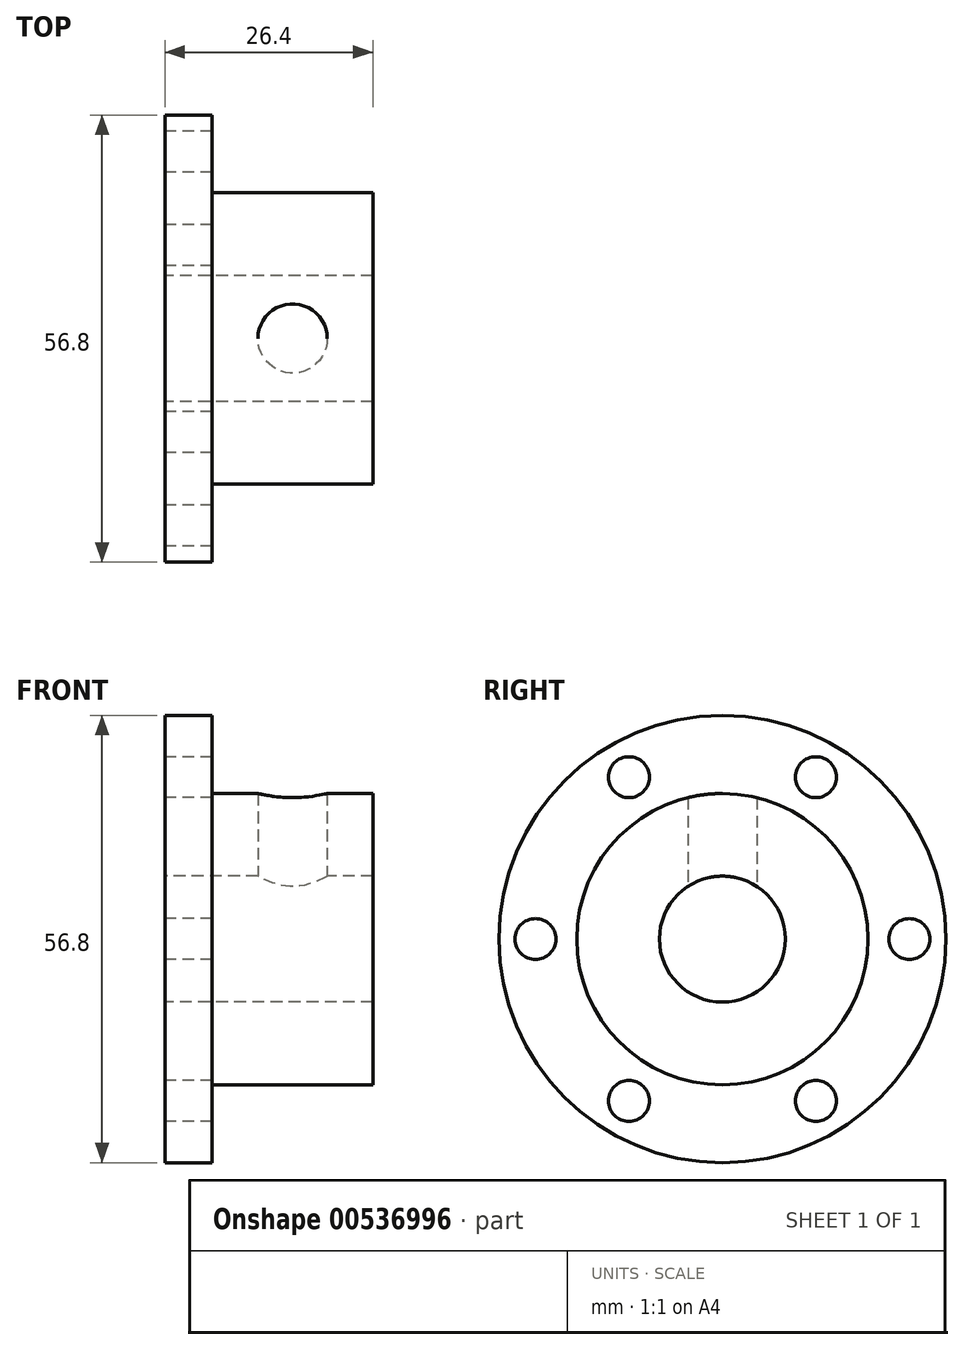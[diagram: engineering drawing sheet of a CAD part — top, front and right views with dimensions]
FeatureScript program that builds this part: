
annotation { "Feature Type Name" : "Feature", "Feature Type Description" : "" }
export const myFeature = defineFeature(function(context is Context, id is Id, definition is map)
    precondition{}
    {
        {
            var Q0;
            Q0=qCreatedBy(makeId("Front.planeOp"),FACE);
            var sketch = newSketch(context, id + "F0", { "sketchPlane" : qUnion([Q0])});
            skLineSegment(sketch, "E0", {"start": v(-27.35, -12.22) * mm, "end": v(29.45, -12.22) * mm});
            skSolve(sketch);
        }
        {
            var Q0;
            Q0=qCreatedBy(makeId("Front.planeOp"),FACE);
            var sketch = newSketch(context, id + "F1", { "sketchPlane" : qUnion([Q0])});
            skLineSegment(sketch, "E1.0", {"start": v(-27.35, -4.22) * mm, "end": v(-0.95, -4.22) * mm});
            skLineSegment(sketch, "E2.0", {"start": v(-21.35, 6.28) * mm, "end": v(-0.95, 6.28) * mm});
            skLineSegment(sketch, "E3.0", {"start": v(-27.35, 16.18) * mm, "end": v(-21.35, 16.18) * mm});
            skLineSegment(sketch, "E4", {"start": v(-27.35, 16.18) * mm, "end": v(-27.35, -4.22) * mm});
            skLineSegment(sketch, "E5.0", {"start": v(-21.35, 16.18) * mm, "end": v(-21.35, 6.28) * mm});
            skLineSegment(sketch, "E6.0", {"start": v(-0.95, 6.28) * mm, "end": v(-0.95, -4.22) * mm});
            skSolve(sketch);
        }
        {
            var Q0;
            Q0=makeQuery(id+"F1.imprint","IMPRINT",FACE,{"disambiguationData":[TD([[makeQuery(id+"F1.imprint","IMPRINT",EDGE,{"derivedFrom":sQuery(id+"F1.wireOp",EDGE,"E1.0")}),1.0]])]});
            var Q1;
            Q1=sQuery(id+"F0.wireOp",EDGE,"E0");
            revolve(context, id + "F2", {"entities" : qUnion([Q0]), "axis" : qUnion([Q1]), "revolveType" : RevolveType.FULL});
        }
        {
            var Q0;
            Q0=makeQuery(id+"F2.opRevolve","SWEPT_FACE",FACE,{"disambiguationData":[OSD([sQuery(id+"F1.wireOp",EDGE,"E4")])]});
            var sketch = newSketch(context, id + "F3", { "sketchPlane" : qUnion([Q0])});
            skLineSegment(sketch, "E7", {"start": v(0, -12.22) * mm, "end": v(23.75, -12.22) * mm});
            skCircle(sketch, "E8", {"center": v(23.75, -12.22) * mm, "radius": 2.6 * mm});
            skCircle(sketch, "E9.1.0", {"center": v(11.88, 8.35) * mm, "radius": 2.6 * mm});
            skCircle(sketch, "E9.2.0", {"center": v(-11.87, 8.35) * mm, "radius": 2.6 * mm});
            skCircle(sketch, "E9.3.0", {"center": v(-23.75, -12.22) * mm, "radius": 2.6 * mm});
            skCircle(sketch, "E9.4.0", {"center": v(-11.88, -32.79) * mm, "radius": 2.6 * mm});
            skCircle(sketch, "E9.5.0", {"center": v(11.88, -32.79) * mm, "radius": 2.6 * mm});
            skPoint(sketch, "E9.center", {"position": v(0, -12.22) * mm});
            skSolve(sketch);
        }
        {
            var Q0;
            Q0=makeQuery(id+"F3.imprint","IMPRINT",FACE,{"disambiguationData":[TD([[makeQuery(id+"F3.imprint","IMPRINT",EDGE,{"derivedFrom":sQuery(id+"F3.wireOp",EDGE,"E9.2.0")}),1.0]])]});
            var Q1;
            Q1=makeQuery(id+"F3.imprint","IMPRINT",FACE,{"disambiguationData":[TD([[makeQuery(id+"F3.imprint","IMPRINT",EDGE,{"derivedFrom":sQuery(id+"F3.wireOp",EDGE,"E9.3.0")}),1.0]])]});
            var Q2;
            Q2=makeQuery(id+"F3.imprint","IMPRINT",FACE,{"disambiguationData":[TD([[makeQuery(id+"F3.imprint","IMPRINT",EDGE,{"derivedFrom":sQuery(id+"F3.wireOp",EDGE,"E9.4.0")}),1.0]])]});
            var Q3;
            Q3=makeQuery(id+"F3.imprint","IMPRINT",FACE,{"disambiguationData":[TD([[makeQuery(id+"F3.imprint","IMPRINT",EDGE,{"derivedFrom":sQuery(id+"F3.wireOp",EDGE,"E9.5.0")}),1.0]])]});
            var Q4;
            Q4=makeQuery(id+"F3.imprint","IMPRINT",FACE,{"disambiguationData":[TD([[makeQuery(id+"F3.imprint","IMPRINT",EDGE,{"derivedFrom":sQuery(id+"F3.wireOp",EDGE,"E8")}),1.0]])]});
            var Q5;
            Q5=makeQuery(id+"F3.imprint","IMPRINT",FACE,{"disambiguationData":[TD([[makeQuery(id+"F3.imprint","IMPRINT",EDGE,{"derivedFrom":sQuery(id+"F3.wireOp",EDGE,"E9.1.0")}),1.0]])]});
            extrude(context, id + "F4", {"entities" : qUnion([Q0, Q1, Q2, Q3, Q4, Q5]), "operationType" : NewBodyOperationType.REMOVE, "endBound" : BoundingType.THROUGH_ALL, "oppositeDirection" : true, "depth" : 25 * mm, "offsetDistance" : 25 * mm});
        }
        {
            var Q0;
            Q0=qCreatedBy(makeId("Top.planeOp"),FACE);
            var sketch = newSketch(context, id + "F5", { "sketchPlane" : qUnion([Q0])});
            skLineSegment(sketch, "E10", {"start": v(-0.95, 0) * mm, "end": v(-11.15, 0) * mm});
            skCircle(sketch, "E11", {"center": v(-11.15, 0) * mm, "radius": 4 * mm});
            skSolve(sketch);
        }
        {
            var Q0;
            Q0=sQuery(id+"F5.wireOp",VERTEX,"E11.center");
            var Q1;
            Q1=makeQuery(id+"F2.opRevolve","SWEPT_BODY",BODY,{"disambiguationData":[OSD([sQuery(id+"F1.wireOp",EDGE,"E1.0"),sQuery(id+"F1.wireOp",EDGE,"E2.0"),sQuery(id+"F1.wireOp",EDGE,"E3.0"),sQuery(id+"F1.wireOp",EDGE,"E4"),sQuery(id+"F1.wireOp",EDGE,"E5.0"),sQuery(id+"F1.wireOp",EDGE,"E6.0")])]});
            hole(context, id + "F6", {"style" : HoleStyle.SIMPLE, "endStyle" : HoleEndStyle.THROUGH, "oppositeDirection" : true, "standardTappedOrClearance" : lookupTablePath({ "standard" : "ISO", "fit" : "Normal", "size" : "M8", "type" : "Clearance" }), "standardBlindInLast" : lookupTablePath({ "fit" : "Standard", "standard" : "ISO", "size" : "M8", "type" : "Clearance" }), "holeDiameter" : 8.8 * mm, "isTappedThrough" : true, "tappedDepth" : 12 * mm, "tapClearance" : 3, "locations" : qUnion([Q0]), "scope" : qUnion([Q1])});
        }
        {
            var Q0;
            Q0=sQuery(id+"F5.wireOp",VERTEX,"E11.center");
            var Q1;
            Q1=makeQuery(id+"F2.opRevolve","SWEPT_BODY",BODY,{"disambiguationData":[OSD([sQuery(id+"F1.wireOp",EDGE,"E1.0"),sQuery(id+"F1.wireOp",EDGE,"E2.0"),sQuery(id+"F1.wireOp",EDGE,"E3.0"),sQuery(id+"F1.wireOp",EDGE,"E4"),sQuery(id+"F1.wireOp",EDGE,"E5.0"),sQuery(id+"F1.wireOp",EDGE,"E6.0")])]});
            hole(context, id + "F7", {"style" : HoleStyle.SIMPLE, "endStyle" : HoleEndStyle.BLIND, "standardTappedOrClearance" : lookupTablePath({ "standard" : "ISO", "fit" : "Normal", "size" : "M8", "type" : "Clearance" }), "standardBlindInLast" : lookupTablePath({ "fit" : "Standard", "standard" : "ISO", "size" : "M8", "type" : "Clearance" }), "holeDiameter" : 8.8 * mm, "holeDepth" : 15.75 * mm, "isTappedThrough" : true, "tappedDepth" : 12 * mm, "tapClearance" : 3, "locations" : qUnion([Q0]), "scope" : qUnion([Q1])});
        }
    });
